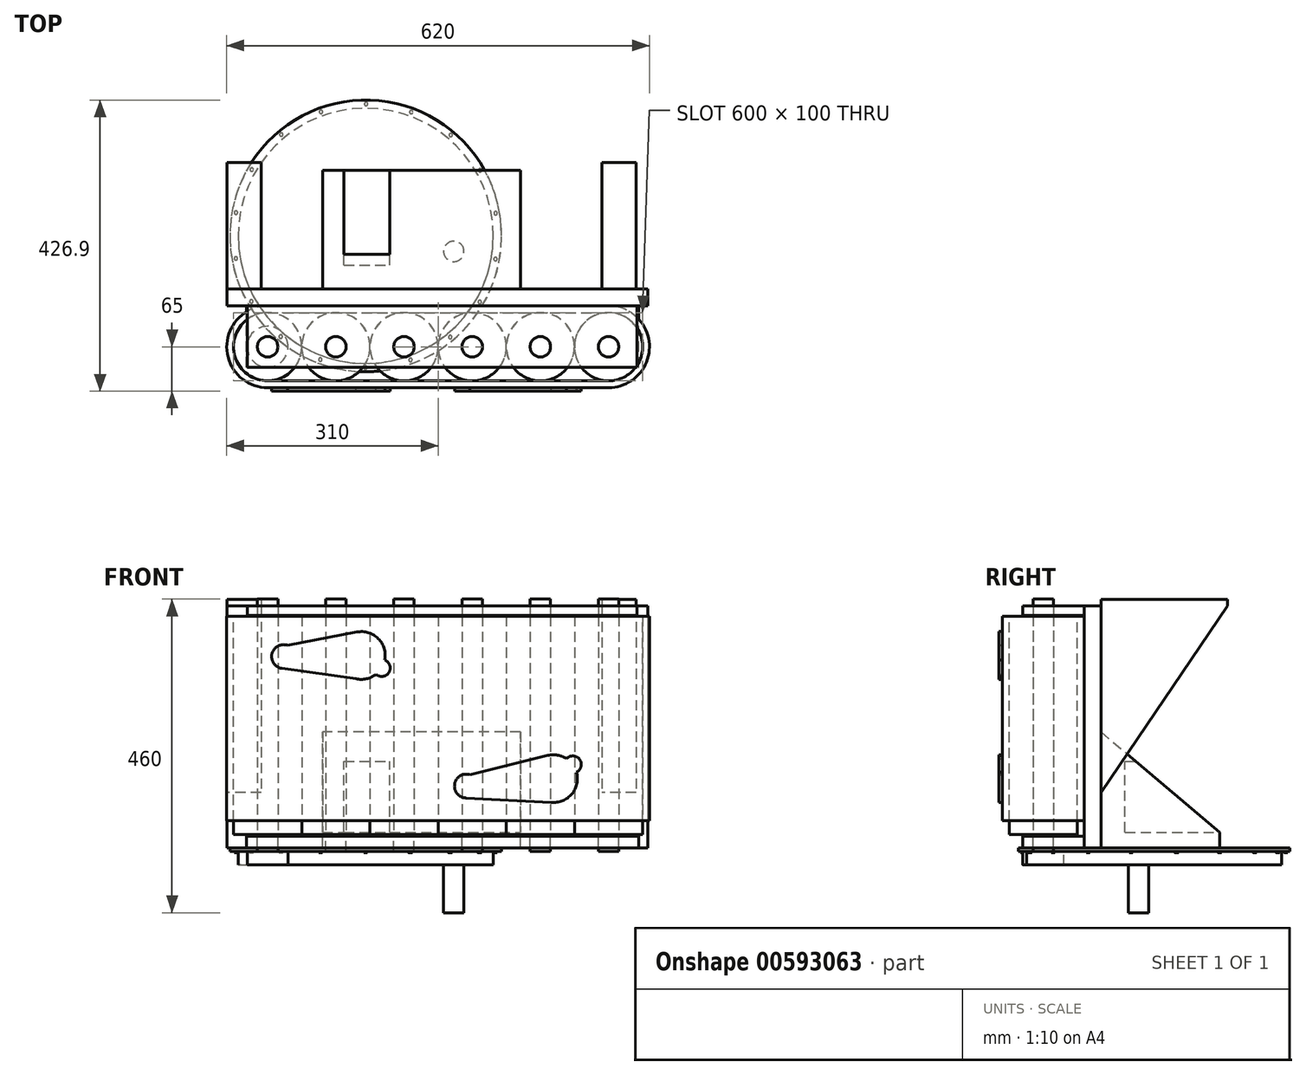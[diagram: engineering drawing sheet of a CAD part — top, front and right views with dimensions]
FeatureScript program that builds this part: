
annotation { "Feature Type Name" : "Feature", "Feature Type Description" : "" }
export const myFeature = defineFeature(function(context is Context, id is Id, definition is map)
    precondition{}
    {
        {
            var Q0;
            Q0=qCreatedBy(makeId("Top.planeOp"),FACE);
            var sketch = newSketch(context, id + "F0", { "sketchPlane" : qUnion([Q0])});
            skCircle(sketch, "E0", {"center": v(0, 0) * mm, "radius": 50 * mm});
            skLineSegment(sketch, "E1", {"start": v(0, 0) * mm, "end": v(100, 0) * mm, "construction": true});
            skCircle(sketch, "E2", {"center": v(100, 0) * mm, "radius": 50 * mm});
            skLineSegment(sketch, "E3", {"start": v(100, 0) * mm, "end": v(200, 0) * mm, "construction": true});
            skLineSegment(sketch, "E4", {"start": v(200, 0) * mm, "end": v(300, 0) * mm, "construction": true});
            skLineSegment(sketch, "E5", {"start": v(300, 0) * mm, "end": v(400, 0) * mm, "construction": true});
            skLineSegment(sketch, "E6", {"start": v(400, 0) * mm, "end": v(500, 0) * mm, "construction": true});
            skCircle(sketch, "E7", {"center": v(200, 0) * mm, "radius": 50 * mm});
            skCircle(sketch, "E8", {"center": v(300, 0) * mm, "radius": 50 * mm});
            skCircle(sketch, "E9", {"center": v(400, 0) * mm, "radius": 50 * mm});
            skCircle(sketch, "E10", {"center": v(500, 0) * mm, "radius": 50 * mm});
            skSolve(sketch);
        }
        {
            var Q0;
            Q0=qSketchRegion(id+"F0",true);
            extrude(context, id + "F1", {"entities" : qUnion([Q0]), "depth" : 300 * mm, "offsetDistance" : 25 * mm});
        }
        {
            var Q0;
            Q0=qSketchRegion(id+"F0",true);
            extrude(context, id + "F2", {"entities" : qUnion([Q0]), "oppositeDirection" : true, "depth" : 20 * mm, "offsetDistance" : 25 * mm});
        }
        {
            var Q0;
            Q0=makeQuery(id+"F2.opExtrude","CAP_FACE",FACE,{"disambiguationData":[OSD([sQuery(id+"F0.wireOp",EDGE,"E0")])],"isStart":false});
            var sketch = newSketch(context, id + "F3", { "sketchPlane" : qUnion([Q0])});
            skCircle(sketch, "E11", {"center": v(0, 0) * mm, "radius": 15 * mm});
            skCircle(sketch, "E12", {"center": v(100, 0) * mm, "radius": 15 * mm});
            skCircle(sketch, "E13", {"center": v(200, 0) * mm, "radius": 15 * mm});
            skCircle(sketch, "E14", {"center": v(300, 0) * mm, "radius": 15 * mm});
            skCircle(sketch, "E15", {"center": v(400, 0) * mm, "radius": 15 * mm});
            skCircle(sketch, "E16", {"center": v(500, 0) * mm, "radius": 15 * mm});
            skSolve(sketch);
        }
        {
            var Q0;
            Q0=qSketchRegion(id+"F3",true);
            extrude(context, id + "F4", {"entities" : qUnion([Q0]), "depth" : 25 * mm, "offsetDistance" : 25 * mm});
        }
        {
            var Q0;
            Q0=qSketchRegion(id+"F3",true);
            extrude(context, id + "F5", {"entities" : qUnion([Q0]), "oppositeDirection" : true, "depth" : 345 * mm, "offsetDistance" : 25 * mm});
        }
        {
            var Q0;
            Q0=makeQuery(id+"F4.opExtrude","CAP_FACE",FACE,{"disambiguationData":[OSD([sQuery(id+"F3.wireOp",EDGE,"E11")])],"isStart":false});
            var sketch = newSketch(context, id + "F6", { "sketchPlane" : qUnion([Q0])});
            skCircle(sketch, "E17", {"center": v(0, 0) * mm, "radius": 30 * mm});
            skSolve(sketch);
        }
        {
            var Q0;
            Q0=qSketchRegion(id+"F6",true);
            extrude(context, id + "F7", {"entities" : qUnion([Q0]), "depth" : 20 * mm, "offsetDistance" : 25 * mm});
        }
        {
            var Q0;
            Q0=makeQuery(id+"F1.opExtrude","CAP_FACE",FACE,{"disambiguationData":[OSD([sQuery(id+"F0.wireOp",EDGE,"E0")])],"isStart":false});
            var sketch = newSketch(context, id + "F8", { "sketchPlane" : qUnion([Q0])});
            skArc(sketch, "E18", {"start": v(0, 60) * mm, "mid": v(-60, 0) * mm, "end": v(0, -60) * mm});
            skLineSegment(sketch, "E19", {"start": v(0, 60) * mm, "end": v(500, 60) * mm});
            skLineSegment(sketch, "E20", {"start": v(0, -60) * mm, "end": v(500, -60) * mm});
            skArc(sketch, "E21", {"start": v(500, -60) * mm, "mid": v(560, 0) * mm, "end": v(500, 60) * mm});
            skLineSegment(sketch, "E22.0", {"start": v(0, 50) * mm, "end": v(500, 50) * mm});
            skArc(sketch, "E22.1", {"start": v(0, 50) * mm, "mid": v(-50, 0) * mm, "end": v(0, -50) * mm});
            skLineSegment(sketch, "E22.2", {"start": v(0, -50) * mm, "end": v(500, -50) * mm});
            skArc(sketch, "E22.3", {"start": v(500, -50) * mm, "mid": v(550, 0) * mm, "end": v(500, 50) * mm});
            skSolve(sketch);
        }
        {
            var Q0;
            Q0=qSketchRegion(id+"F8",true);
            extrude(context, id + "F9", {"entities" : qUnion([Q0]), "oppositeDirection" : true, "depth" : 300 * mm, "offsetDistance" : 25 * mm});
        }
        {
            var Q0;
            Q0=makeQuery(id+"F9.opExtrude","SWEPT_FACE",FACE,{"disambiguationData":[OSD([sQuery(id+"F8.wireOp",EDGE,"E19")])]});
            var sketch = newSketch(context, id + "F10", { "sketchPlane" : qUnion([Q0])});
            skLineSegment(sketch, "E23.bottom", {"start": v(-557.83, 314.73) * mm, "end": v(59.54, 314.73) * mm});
            skLineSegment(sketch, "E23.top", {"start": v(-557.83, -40.11) * mm, "end": v(59.54, -40.11) * mm});
            skLineSegment(sketch, "E23.left", {"start": v(-557.83, 314.73) * mm, "end": v(-557.83, -40.11) * mm});
            skLineSegment(sketch, "E23.right", {"start": v(59.54, 314.73) * mm, "end": v(59.54, -40.11) * mm});
            skSolve(sketch);
        }
        {
            var Q0;
            Q0 = qSketchRegion(id + "F10", true);
            extrude(context, id + "F11", {"entities" : qUnion([Q0]), "depth" : 25 * mm, "offsetDistance" : 25 * mm});
        }
        {
            var Q0;
            Q0=makeQuery(id+"F11.opExtrude","CAP_FACE",FACE,{"disambiguationData":[OSD([sQuery(id+"F10.wireOp",EDGE,"E23.bottom"),sQuery(id+"F10.wireOp",EDGE,"E23.top"),sQuery(id+"F10.wireOp",EDGE,"E23.left"),sQuery(id+"F10.wireOp",EDGE,"E23.right")])],"isStart":true});
            var sketch = newSketch(context, id + "F12", { "sketchPlane" : qUnion([Q0])});
            skLineSegment(sketch, "E24.bottom", {"start": v(-29.86, 314.73) * mm, "end": v(541.7, 314.73) * mm});
            skLineSegment(sketch, "E24.top", {"start": v(-29.86, 301.06) * mm, "end": v(541.7, 301.06) * mm});
            skLineSegment(sketch, "E24.left", {"start": v(-29.86, 314.73) * mm, "end": v(-29.86, 301.06) * mm});
            skLineSegment(sketch, "E24.right", {"start": v(541.7, 314.73) * mm, "end": v(541.7, 301.06) * mm});
            skSolve(sketch);
        }
        {
            var Q0;
            Q0 = qSketchRegion(id + "F12", true);
            extrude(context, id + "F13", {"entities" : qUnion([Q0]), "depth" : 90 * mm, "offsetDistance" : 25 * mm});
        }
        {
            var Q0;
            Q0=makeQuery(id+"F11.opExtrude","CAP_FACE",FACE,{"disambiguationData":[OSD([sQuery(id+"F10.wireOp",EDGE,"E23.bottom"),sQuery(id+"F10.wireOp",EDGE,"E23.top"),sQuery(id+"F10.wireOp",EDGE,"E23.left"),sQuery(id+"F10.wireOp",EDGE,"E23.right")])],"isStart":true});
            var sketch = newSketch(context, id + "F14", { "sketchPlane" : qUnion([Q0])});
            skLineSegment(sketch, "E25.bottom", {"start": v(-31.35, -22.85) * mm, "end": v(544.26, -22.85) * mm});
            skLineSegment(sketch, "E25.top", {"start": v(-31.35, -40.11) * mm, "end": v(544.26, -40.11) * mm});
            skLineSegment(sketch, "E25.left", {"start": v(-31.35, -22.85) * mm, "end": v(-31.35, -40.11) * mm});
            skLineSegment(sketch, "E25.right", {"start": v(544.26, -22.85) * mm, "end": v(544.26, -40.11) * mm});
            skSolve(sketch);
        }
        {
            var Q0;
            Q0 = qSketchRegion(id + "F14", true);
            extrude(context, id + "F15", {"entities" : qUnion([Q0]), "depth" : 90 * mm, "offsetDistance" : 25 * mm});
        }
        {
            var Q0;
            Q0=makeQuery(id+"F11.opExtrude","SWEPT_FACE",FACE,{"disambiguationData":[OSD([sQuery(id+"F10.wireOp",EDGE,"E23.right")])]});
            var sketch = newSketch(context, id + "F16", { "sketchPlane" : qUnion([Q0])});
            skLineSegment(sketch, "E26", {"start": v(-85, 41.27) * mm, "end": v(-270.2, 314.73) * mm});
            skLineSegment(sketch, "E27", {"start": v(-270.2, 314.73) * mm, "end": v(-85, 314.73) * mm});
            skLineSegment(sketch, "E28", {"start": v(-85, 314.73) * mm, "end": v(-85, 41.27) * mm});
            skSolve(sketch);
        }
        {
            var Q0;
            Q0 = qSketchRegion(id + "F16", true);
            extrude(context, id + "F17", {"entities" : qUnion([Q0]), "oppositeDirection" : true, "depth" : 50 * mm, "offsetDistance" : 25 * mm});
        }
        {
            var Q0;
            Q0=makeQuery(id+"F17.opExtrude","SWEPT_BODY",BODY,{"disambiguationData":[OSD([sQuery(id+"F16.wireOp",EDGE,"E26"),sQuery(id+"F16.wireOp",EDGE,"E27"),sQuery(id+"F16.wireOp",EDGE,"E28")])]});
            transform(context, id + "F18", {"entities" : qUnion([Q0]), "transformType" : TransformType.TRANSLATION_3D, "dx" : 550 * mm, "dy" : 0 * mm, "dz" : 0 * mm, "makeCopy" : true});
        }
        {
            var Q0;
            Q0=makeQuery(id+"F11.opExtrude","CAP_FACE",FACE,{"disambiguationData":[OSD([sQuery(id+"F10.wireOp",EDGE,"E23.bottom"),sQuery(id+"F10.wireOp",EDGE,"E23.top"),sQuery(id+"F10.wireOp",EDGE,"E23.left"),sQuery(id+"F10.wireOp",EDGE,"E23.right")])],"isStart":false});
            var sketch = newSketch(context, id + "F19", { "sketchPlane" : qUnion([Q0])});
            skLineSegment(sketch, "E29.bottom", {"start": v(-80.5, -40.11) * mm, "end": v(-370.82, -40.11) * mm});
            skLineSegment(sketch, "E29.top", {"start": v(-80.5, -17.08) * mm, "end": v(-370.82, -17.08) * mm});
            skLineSegment(sketch, "E29.left", {"start": v(-80.5, -40.11) * mm, "end": v(-80.5, -17.08) * mm});
            skLineSegment(sketch, "E29.right", {"start": v(-370.82, -40.11) * mm, "end": v(-370.82, -17.08) * mm});
            skSolve(sketch);
        }
        {
            var Q0;
            Q0 = qSketchRegion(id + "F19", true);
            extrude(context, id + "F20", {"entities" : qUnion([Q0]), "operationType" : NewBodyOperationType.ADD, "depth" : 174 * mm, "offsetDistance" : 25 * mm});
        }
        {
            var Q0;
            Q0=makeQuery(id+"F20.opExtrude","SWEPT_FACE",FACE,{"disambiguationData":[OSD([sQuery(id+"F19.wireOp",EDGE,"E29.left")])]});
            var sketch = newSketch(context, id + "F21", { "sketchPlane" : qUnion([Q0])});
            skLineSegment(sketch, "E30", {"start": v(-259, -17.08) * mm, "end": v(-85, -17.08) * mm});
            skLineSegment(sketch, "E31", {"start": v(-85, -17.08) * mm, "end": v(-85, 129.88) * mm});
            skLineSegment(sketch, "E32", {"start": v(-85, 129.88) * mm, "end": v(-259, -17.08) * mm});
            skSolve(sketch);
        }
        {
            var Q0;
            Q0 = qSketchRegion(id + "F21", true);
            var Q1;
            Q1=makeQuery(id+"F20.opExtrude","SWEPT_FACE",FACE,{"disambiguationData":[OSD([sQuery(id+"F19.wireOp",EDGE,"E29.right")])]});
            extrude(context, id + "F22", {"entities" : qUnion([Q0]), "operationType" : NewBodyOperationType.ADD, "endBound" : BoundingType.UP_TO_SURFACE, "oppositeDirection" : true, "depth" : 256 * mm, "endBoundEntityFace" : qUnion([Q1]), "offsetDistance" : 25 * mm});
        }
        {
            var Q0;
            Q0=makeQuery(id+"F7.opExtrude","CAP_FACE",FACE,{"disambiguationData":[OSD([sQuery(id+"F6.wireOp",EDGE,"E17")])],"isStart":false});
            var sketch = newSketch(context, id + "F23", { "sketchPlane" : qUnion([Q0])});
            skCircle(sketch, "E33", {"center": v(143.87, -162.67) * mm, "radius": 187.16 * mm});
            skSolve(sketch);
        }
        {
            var Q0;
            Q0 = qSketchRegion(id + "F23", true);
            extrude(context, id + "F24", {"entities" : qUnion([Q0]), "oppositeDirection" : true, "depth" : 20 * mm, "offsetDistance" : 25 * mm});
        }
        {
            var Q0;
            Q0=makeQuery(id+"F24.opExtrude","CAP_FACE",FACE,{"disambiguationData":[OSD([sQuery(id+"F23.wireOp",EDGE,"E33")])],"isStart":true});
            var sketch = newSketch(context, id + "F25", { "sketchPlane" : qUnion([Q0])});
            skCircle(sketch, "E34", {"center": v(273, -139.89) * mm, "radius": 15 * mm});
            skSolve(sketch);
        }
        {
            var Q0;
            Q0 = qSketchRegion(id + "F25", true);
            extrude(context, id + "F26", {"entities" : qUnion([Q0]), "operationType" : NewBodyOperationType.ADD, "depth" : 70 * mm, "offsetDistance" : 25 * mm});
        }
        {
            var Q0;
            Q0=makeQuery(id+"F9.opExtrude","SWEPT_FACE",FACE,{"disambiguationData":[OSD([sQuery(id+"F8.wireOp",EDGE,"E20")])]});
            var sketch = newSketch(context, id + "F27", { "sketchPlane" : qUnion([Q0])});
            skCircle(sketch, "E35", {"center": v(291.56, 50.75) * mm, "radius": 17.5 * mm});
            skCircle(sketch, "E36", {"center": v(419.34, 61.67) * mm, "radius": 35 * mm});
            skLineSegment(sketch, "E37", {"start": v(296.9, 67.41) * mm, "end": v(410.93, 95.65) * mm});
            skLineSegment(sketch, "E38", {"start": v(410.93, 95.65) * mm, "end": v(419.34, 26.67) * mm});
            skLineSegment(sketch, "E39", {"start": v(419.34, 26.67) * mm, "end": v(290.66, 33.27) * mm});
            skCircle(sketch, "E40", {"center": v(447.5, 82.44) * mm, "radius": 12.5 * mm});
            skLineSegment(sketch, "E41", {"start": v(500, 150) * mm, "end": v(0, 150) * mm, "construction": true});
            skLineSegment(sketch, "E42", {"start": v(0, 150) * mm, "end": v(250, 0) * mm, "construction": true});
            skLineSegment(sketch, "E43", {"start": v(250, 0) * mm, "end": v(250, 300) * mm, "construction": true});
            skCircle(sketch, "E44", {"center": v(167.26, 224) * mm, "radius": 12.5 * mm});
            skCircle(sketch, "E45", {"center": v(137.38, 242.23) * mm, "radius": 35 * mm});
            skCircle(sketch, "E46", {"center": v(23.33, 240.62) * mm, "radius": 17.5 * mm});
            skLineSegment(sketch, "E47", {"start": v(29.11, 257.14) * mm, "end": v(130.8, 276.6) * mm});
            skLineSegment(sketch, "E48", {"start": v(135.48, 207.28) * mm, "end": v(20.9, 223.3) * mm});
            skSolve(sketch);
        }
        {
            var Q0;
            Q0 = qSketchRegion(id + "F27", true);
            extrude(context, id + "F28", {"entities" : qUnion([Q0]), "depth" : 5 * mm, "offsetDistance" : 25 * mm});
        }
        {
            var Q0;
            Q0=makeQuery(id+"F24.opExtrude","CAP_FACE",FACE,{"disambiguationData":[OSD([sQuery(id+"F23.wireOp",EDGE,"E33")])],"isStart":false});
            var sketch = newSketch(context, id + "F29", { "sketchPlane" : qUnion([Q0])});
            skCircle(sketch, "E49", {"center": v(143.87, 162.67) * mm, "radius": 199.23 * mm});
            skSolve(sketch);
        }
        {
            var Q0;
            Q0 = qSketchRegion(id + "F29", true);
            extrude(context, id + "F30", {"entities" : qUnion([Q0]), "depth" : 5 * mm, "offsetDistance" : 25 * mm});
        }
        {
            var Q0;
            Q0=makeQuery(id+"F30.opExtrude","CAP_FACE",FACE,{"disambiguationData":[OSD([sQuery(id+"F29.wireOp",EDGE,"E49")])],"isStart":true});
            var sketch = newSketch(context, id + "F31", { "sketchPlane" : qUnion([Q0])});
            skCircle(sketch, "E50", {"center": v(143.36, 30.69) * mm, "radius": 2.5 * mm});
            skSolve(sketch);
        }
        {
            var Q0;
            Q0 = qSketchRegion(id + "F31", true);
            extrude(context, id + "F32", {"entities" : qUnion([Q0]), "depth" : 2 * mm, "offsetDistance" : 25 * mm});
        }
        {
            var Q0;
            Q0=makeQuery(id+"F32.opExtrude","SWEPT_BODY",BODY,{"disambiguationData":[OSD([sQuery(id+"F31.wireOp",EDGE,"E50")])]});
            var Q1;
            Q1=makeQuery(id+"F24.opExtrude","CAP_EDGE",EDGE,{"disambiguationData":[OSD([sQuery(id+"F23.wireOp",EDGE,"E33")])],"isStart":true});
            circularPattern(context, id + "F33", {"entities" : qUnion([Q0]), "axis" : qUnion([Q1]), "angle" : 360 * degree, "instanceCount" : 18, "equalSpace" : true});
        }
        {
            var Q0;
            Q0=makeQuery(id+"F18.opPattern","COPY",FACE,{"derivedFrom":makeQuery(id+"F17.opExtrude","SWEPT_FACE",FACE,{"disambiguationData":[OSD([sQuery(id+"F16.wireOp",EDGE,"E27")])]}),"instanceName":"1"});
            var sketch = newSketch(context, id + "F34", { "sketchPlane" : qUnion([Q0])});
            skLineSegment(sketch, "E51.bottom", {"start": v(540.46, 270.2) * mm, "end": v(490.46, 270.2) * mm});
            skLineSegment(sketch, "E51.top", {"start": v(540.46, 85) * mm, "end": v(490.46, 85) * mm});
            skLineSegment(sketch, "E51.left", {"start": v(540.46, 270.2) * mm, "end": v(540.46, 85) * mm});
            skLineSegment(sketch, "E51.right", {"start": v(490.46, 270.2) * mm, "end": v(490.46, 85) * mm});
            skSolve(sketch);
        }
        {
            var Q0;
            Q0=makeQuery(id+"F34.imprint","IMPRINT",FACE,{"disambiguationData":[TD([[makeQuery(id+"F34.imprint","IMPRINT",EDGE,{"derivedFrom":sQuery(id+"F34.wireOp",EDGE,"E51.bottom")}),1.0]])]});
            extrude(context, id + "F35", {"entities" : qUnion([Q0]), "operationType" : NewBodyOperationType.ADD, "depth" : 10 * mm, "offsetDistance" : 25 * mm});
        }
        {
            var Q0;
            Q0=makeQuery(id+"F17.opExtrude","SWEPT_FACE",FACE,{"disambiguationData":[OSD([sQuery(id+"F16.wireOp",EDGE,"E27")])]});
            var sketch = newSketch(context, id + "F36", { "sketchPlane" : qUnion([Q0])});
            skLineSegment(sketch, "E52.bottom", {"start": v(-59.54, 270.2) * mm, "end": v(-9.54, 270.2) * mm});
            skLineSegment(sketch, "E52.top", {"start": v(-59.54, 85) * mm, "end": v(-9.54, 85) * mm});
            skLineSegment(sketch, "E52.left", {"start": v(-59.54, 270.2) * mm, "end": v(-59.54, 85) * mm});
            skLineSegment(sketch, "E52.right", {"start": v(-9.54, 270.2) * mm, "end": v(-9.54, 85) * mm});
            skSolve(sketch);
        }
        {
            var Q0;
            Q0 = qSketchRegion(id + "F36", true);
            extrude(context, id + "F37", {"entities" : qUnion([Q0]), "operationType" : NewBodyOperationType.ADD, "depth" : 10 * mm, "offsetDistance" : 25 * mm});
        }
        {
            var Q0;
            Q0=makeQuery(id+"F24.opExtrude","CAP_FACE",FACE,{"disambiguationData":[OSD([sQuery(id+"F23.wireOp",EDGE,"E33")])],"isStart":true});
            var sketch = newSketch(context, id + "F38", { "sketchPlane" : qUnion([Q0])});
            skCircle(sketch, "E53", {"center": v(143.87, -162.67) * mm, "radius": 40.17 * mm, "construction": true});
            skCircle(sketch, "E54", {"center": v(143.87, -162.67) * mm, "radius": 10 * mm});
            skSolve(sketch);
        }
        {
            var Q0;
            Q0 = qSketchRegion(id + "F38", true);
            extrude(context, id + "F39", {"entities" : qUnion([Q0]), "operationType" : NewBodyOperationType.ADD, "oppositeDirection" : true, "depth" : 60 * mm, "offsetDistance" : 25 * mm});
        }
        {
            var Q0;
            Q0=makeQuery(id+"F20.opExtrude","CAP_FACE",FACE,{"disambiguationData":[OSD([sQuery(id+"F19.wireOp",EDGE,"E29.bottom"),sQuery(id+"F19.wireOp",EDGE,"E29.top"),sQuery(id+"F19.wireOp",EDGE,"E29.left"),sQuery(id+"F19.wireOp",EDGE,"E29.right")])],"isStart":false});
            var sketch = newSketch(context, id + "F40", { "sketchPlane" : qUnion([Q0])});
            skLineSegment(sketch, "E55.bottom", {"start": v(-111.86, -17.08) * mm, "end": v(-179.19, -17.08) * mm});
            skLineSegment(sketch, "E55.top", {"start": v(-111.86, 87.23) * mm, "end": v(-179.19, 87.23) * mm});
            skLineSegment(sketch, "E55.left", {"start": v(-111.86, -17.08) * mm, "end": v(-111.86, 87.23) * mm});
            skLineSegment(sketch, "E55.right", {"start": v(-179.19, -17.08) * mm, "end": v(-179.19, 87.23) * mm});
            skSolve(sketch);
        }
        {
            var Q0;
            Q0 = qSketchRegion(id + "F40", true);
            extrude(context, id + "F41", {"entities" : qUnion([Q0]), "operationType" : NewBodyOperationType.REMOVE, "oppositeDirection" : true, "depth" : 139 * mm, "offsetDistance" : 25 * mm});
        }
    });
